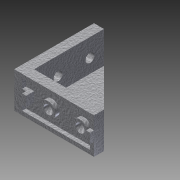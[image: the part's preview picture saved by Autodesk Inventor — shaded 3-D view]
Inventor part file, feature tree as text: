
AUTODESK INVENTOR PART (.ipt)
format: ipt  version: 2015 SP1 (Build 190203100, 203)  size: 215,552 bytes
history: native  units: mm
features: extrude x10, sketch x3, chamfer x2, projected_geometry x2
ambient origin geometry x8: Origin, YZ Plane, XZ Plane, XY Plane, X Axis, Y Axis, Z Axis, Center Point
bodies: Solid1 (feature_tree)
feature tree (17):
  sketch  "Sketch1"  dims[d0=38.0mm d1=3.0mm]
  extrude  "Extrusion1"  Depth=3.0mm
  extrude  "Extrusion2"  Depth=2.0mm TaperAngle=0.0deg
  sketch  "Sketch2"  dims[d2=18.0mm d3=0.0mm d4=2.0mm d5=0.0mm]
  extrude  "Extrusion3"  Depth=2.0mm
  extrude  "Extrusion4"  Depth=2.0mm
  extrude  "Extrusion5"  Depth=2.0mm
  extrude  "Extrusion6"  Depth=5.0mm
  extrude  "Extrusion7"  Depth=4.0mm
  chamfer  "Chamfer1"  Distance=4.5mm
  chamfer  "Chamfer2"  Distance=0.75mm
  sketch  "Sketch3"  dims[d6=2.0mm d7=2.0mm d8=2.0mm d9=2.0mm d10=5.0mm d11=4.0mm d12=4.5mm d13=0.75mm d14=0.75mm d15=16.0mm d16=5.0mm d17=2.0mm d18=0.0mm d19=4.0mm d20=0.0mm d21=4.0mm d22=0.0mm d23=4.0mm d24=0.0mm d25=4.0mm d26=0.0mm d27=2.0mm d28=2.0mm d29=15.0deg d30=2.0mm d31=2.0mm d32=15.0deg d37=5.0mm d38=4.0mm d39=4.5mm d40=0.75mm d41=0.75mm d42=16.0mm d43=5.0mm d44=2.0mm d45=4.0mm d46=2.0mm d47=2.0mm d48=0.0mm d49=4.0mm d50=0.0mm d51=4.0mm d52=0.0mm]
  extrude  "Extrusion8"  Depth=4.0mm
  extrude  "Extrusion9"  Depth=16.0mm
  extrude  "Extrusion10"  Depth=5.0mm
  projected_geometry  "Projected Loop1"
  projected_geometry  "Projected Loop2"
